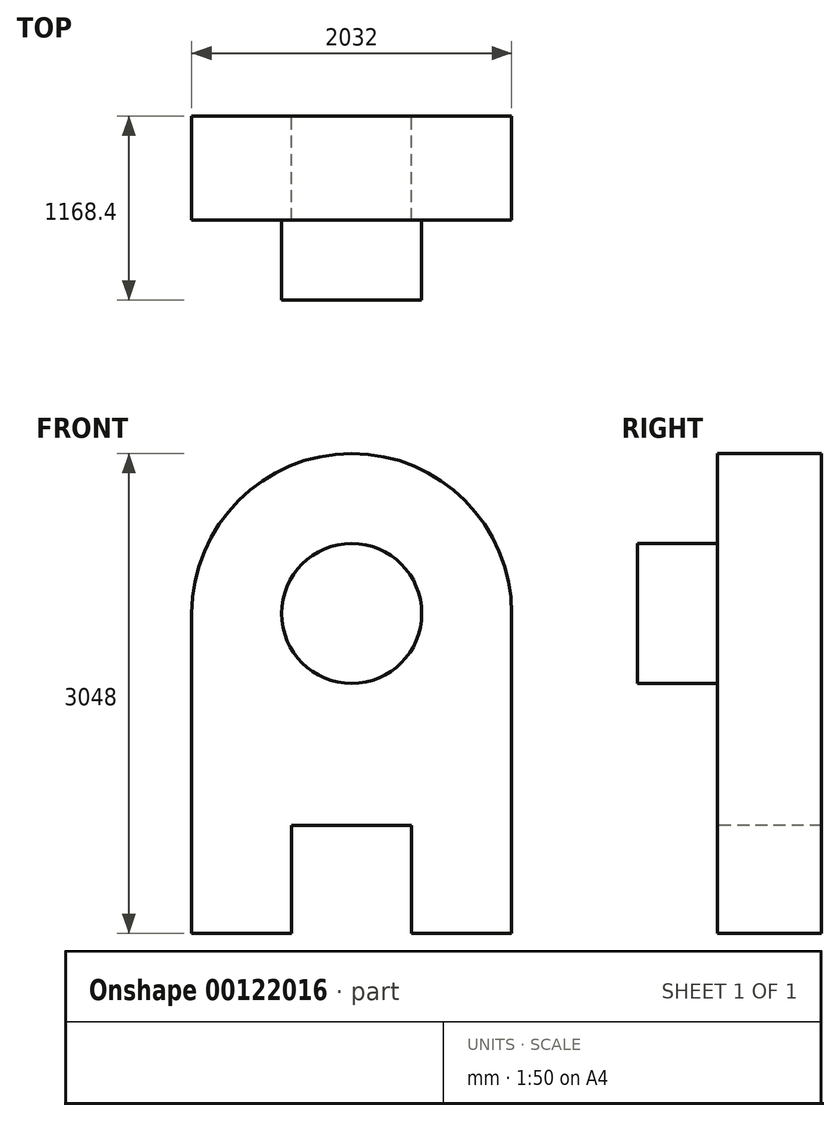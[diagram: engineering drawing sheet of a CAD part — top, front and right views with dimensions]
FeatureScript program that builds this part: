
annotation { "Feature Type Name" : "Feature", "Feature Type Description" : "" }
export const myFeature = defineFeature(function(context is Context, id is Id, definition is map)
    precondition{}
    {
        {
            var Q0;
            Q0=qCreatedBy(makeId("Front.planeOp"),FACE);
            var sketch = newSketch(context, id + "F0", { "sketchPlane" : qUnion([Q0])});
            skLineSegment(sketch, "E0.bottom", {"start": v(1016, -1016) * mm, "end": v(-1016, -1016) * mm});
            skLineSegment(sketch, "E0.top", {"start": v(1016, 1016) * mm, "end": v(-1016, 1016) * mm});
            skLineSegment(sketch, "E0.left", {"start": v(1016, -1016) * mm, "end": v(1016, 1016) * mm});
            skLineSegment(sketch, "E0.right", {"start": v(-1016, -1016) * mm, "end": v(-1016, 1016) * mm});
            skPoint(sketch, "E0.middle", {"position": v(0, 0) * mm});
            skCircle(sketch, "E1", {"center": v(0, 1016) * mm, "radius": 1016 * mm});
            skLineSegment(sketch, "E2.bottom", {"start": v(381, -1651) * mm, "end": v(-381, -1651) * mm});
            skLineSegment(sketch, "E2.top", {"start": v(381, -381) * mm, "end": v(-381, -381) * mm});
            skLineSegment(sketch, "E2.left", {"start": v(381, -1651) * mm, "end": v(381, -381) * mm});
            skLineSegment(sketch, "E2.right", {"start": v(-381, -1651) * mm, "end": v(-381, -381) * mm});
            skPoint(sketch, "E2.middle", {"position": v(0, -1016) * mm});
            skSolve(sketch);
        }
        {
            var Q0;
            {var subQ0=sQuery(id+"F0.wireOp",EDGE,"E0.top");Q0=makeQuery(id+"F0.imprint","IMPRINT",FACE,{"disambiguationData":[TD([[makeQuery(id+"F0.imprint","IMPRINT",EDGE,{"derivedFrom":subQ0}),1.0]])]});}
            var Q1;
            {var subQ5=sQuery(id+"F0.wireOp",EDGE,"E2.bottom");Q1=makeQuery(id+"F0.imprint","IMPRINT",FACE,{"disambiguationData":[TD([[makeQuery(id+"F0.imprint","IMPRINT",EDGE,{"derivedFrom":subQ5}),-1.0]])]});}
            var Q2;
            {var subQ1=sQuery(id+"F0.wireOp",EDGE,"E0.left");Q2=makeQuery(id+"F0.imprint","IMPRINT",FACE,{"disambiguationData":[TD([[makeQuery(id+"F0.imprint","IMPRINT",EDGE,{"derivedFrom":subQ1}),1.0]])]});}
            var Q3;
            {var subQ5=sQuery(id+"F0.wireOp",EDGE,"E2.top");Q3=makeQuery(id+"F0.imprint","IMPRINT",FACE,{"disambiguationData":[TD([[makeQuery(id+"F0.imprint","IMPRINT",EDGE,{"derivedFrom":subQ5}),1.0]])]});}
            var Q4;
            {var subQ0=sQuery(id+"F0.wireOp",EDGE,"E0.top");Q4=makeQuery(id+"F0.imprint","IMPRINT",FACE,{"disambiguationData":[TD([[makeQuery(id+"F0.imprint","IMPRINT",EDGE,{"derivedFrom":subQ0}),-1.0]])]});}
            extrude(context, id + "F1", {"entities" : qUnion([Q0, Q1, Q2, Q3, Q4]), "depth" : 635 * mm});
        }
        {
            var Q0;
            Q0=makeQuery(id+"F1.opExtrude","CAP_FACE",FACE,{"disambiguationData":[OSD([sQuery(id+"F0.wireOp",EDGE,"E0.bottom"),sQuery(id+"F0.wireOp",EDGE,"E0.left"),sQuery(id+"F0.wireOp",EDGE,"E0.right"),sQuery(id+"F0.wireOp",EDGE,"E1"),sQuery(id+"F0.wireOp",EDGE,"E2.bottom"),sQuery(id+"F0.wireOp",EDGE,"E2.left"),sQuery(id+"F0.wireOp",EDGE,"E2.right")])],"isStart":false});
            extrude(context, id + "F2", {"entities" : qUnion([Q0]), "operationType" : NewBodyOperationType.ADD, "depth" : 25.4 * mm});
        }
        {
            var Q0;
            Q0=makeQuery(id+"F2.opExtrude","CAP_FACE",FACE,{"disambiguationData":[OSD([sQuery(id+"F0.wireOp",EDGE,"E0.bottom"),sQuery(id+"F0.wireOp",EDGE,"E0.left"),sQuery(id+"F0.wireOp",EDGE,"E0.right"),sQuery(id+"F0.wireOp",EDGE,"E1"),sQuery(id+"F0.wireOp",EDGE,"E2.bottom"),sQuery(id+"F0.wireOp",EDGE,"E2.left"),sQuery(id+"F0.wireOp",EDGE,"E2.right")])],"isStart":false});
            var sketch = newSketch(context, id + "F3", { "sketchPlane" : qUnion([Q0])});
            skLineSegment(sketch, "E3.bottom", {"start": v(381, -1651) * mm, "end": v(-381, -1651) * mm});
            skLineSegment(sketch, "E3.top", {"start": v(381, -328.47) * mm, "end": v(-381, -328.47) * mm});
            skLineSegment(sketch, "E3.left", {"start": v(381, -1651) * mm, "end": v(381, -328.47) * mm});
            skLineSegment(sketch, "E3.right", {"start": v(-381, -1651) * mm, "end": v(-381, -328.47) * mm});
            skPoint(sketch, "E3.middle", {"position": v(0, -989.73) * mm});
            skSolve(sketch);
        }
        {
            var Q0;
            Q0 = qSketchRegion(id + "F3", true);
            extrude(context, id + "F4", {"entities" : qUnion([Q0]), "operationType" : NewBodyOperationType.REMOVE, "endBound" : BoundingType.THROUGH_ALL, "oppositeDirection" : true, "depth" : 25.4 * mm});
        }
        {
            var Q0;
            Q0=makeQuery(id+"F2.opExtrude","CAP_FACE",FACE,{"disambiguationData":[OSD([sQuery(id+"F0.wireOp",EDGE,"E0.bottom"),sQuery(id+"F0.wireOp",EDGE,"E0.left"),sQuery(id+"F0.wireOp",EDGE,"E0.right"),sQuery(id+"F0.wireOp",EDGE,"E1"),sQuery(id+"F0.wireOp",EDGE,"E2.bottom"),sQuery(id+"F0.wireOp",EDGE,"E2.left"),sQuery(id+"F0.wireOp",EDGE,"E2.right")])],"isStart":false});
            var sketch = newSketch(context, id + "F5", { "sketchPlane" : qUnion([Q0])});
            skCircle(sketch, "E4", {"center": v(0, 1016) * mm, "radius": 444.5 * mm});
            skSolve(sketch);
        }
        {
            var Q0;
            Q0 = qSketchRegion(id + "F5", true);
            extrude(context, id + "F6", {"entities" : qUnion([Q0]), "operationType" : NewBodyOperationType.ADD, "depth" : 508 * mm});
        }
    });
